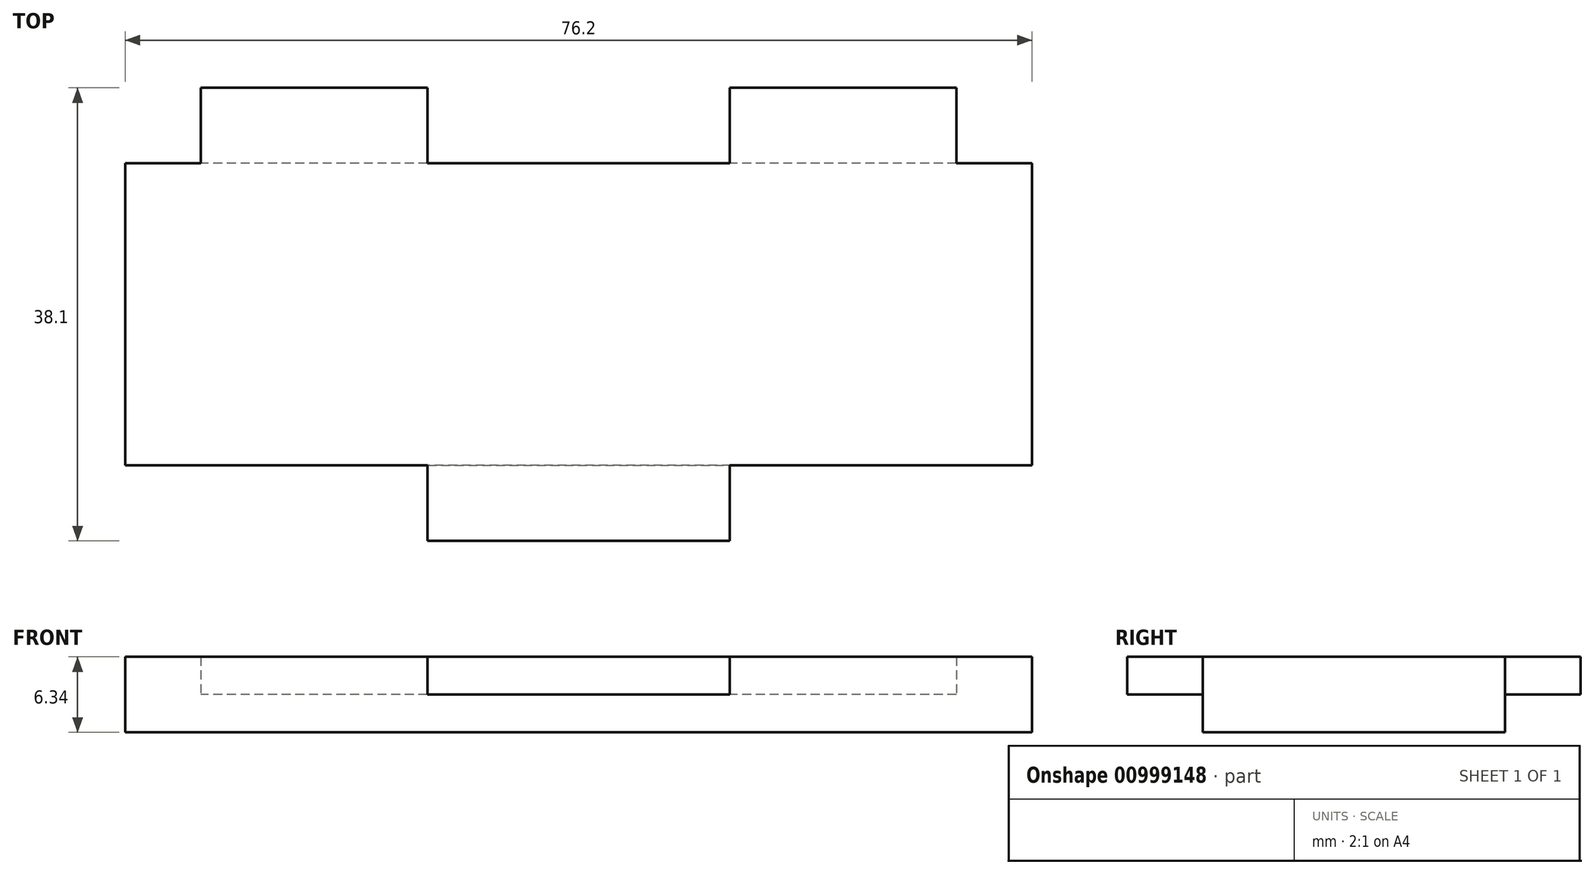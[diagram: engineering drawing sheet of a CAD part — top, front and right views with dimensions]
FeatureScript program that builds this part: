
annotation { "Feature Type Name" : "Feature", "Feature Type Description" : "" }
export const myFeature = defineFeature(function(context is Context, id is Id, definition is map)
    precondition{}
    {
        {
            var Q0;
            Q0=qCreatedBy(makeId("Right.planeOp"),FACE);
            var sketch = newSketch(context, id + "F0", { "sketchPlane" : qUnion([Q0])});
            skLineSegment(sketch, "E0.bottom", {"start": v(12.7, -3.17) * mm, "end": v(-12.7, -3.18) * mm});
            skLineSegment(sketch, "E0.top", {"start": v(12.7, 3.18) * mm, "end": v(-12.7, 3.17) * mm});
            skLineSegment(sketch, "E0.left", {"start": v(12.7, -3.17) * mm, "end": v(12.7, 3.18) * mm});
            skLineSegment(sketch, "E0.right", {"start": v(-12.7, -3.18) * mm, "end": v(-12.7, 3.17) * mm});
            skPoint(sketch, "E0.middle", {"position": v(0, 0) * mm});
            skSolve(sketch);
        }
        {
            var Q0;
            Q0 = qSketchRegion(id + "F0", true);
            extrude(context, id + "F1", {"entities" : qUnion([Q0]), "depth" : 76.2 * mm, "offsetDistance" : 25.4 * mm});
        }
        {
            var Q0;
            Q0=makeQuery(id+"F1.opExtrude","SWEPT_FACE",FACE,{"disambiguationData":[OSD([sQuery(id+"F0.wireOp",EDGE,"E0.right")])]});
            var sketch = newSketch(context, id + "F2", { "sketchPlane" : qUnion([Q0])});
            skLineSegment(sketch, "E1", {"start": v(0, 0) * mm, "end": v(25.4, 0) * mm});
            skLineSegment(sketch, "E2", {"start": v(76.2, 0) * mm, "end": v(50.8, 0) * mm});
            skLineSegment(sketch, "E3.bottom", {"start": v(25.4, 0) * mm, "end": v(50.8, 0) * mm});
            skLineSegment(sketch, "E3.top", {"start": v(25.4, 3.17) * mm, "end": v(50.8, 3.17) * mm});
            skLineSegment(sketch, "E3.left", {"start": v(25.4, 0) * mm, "end": v(25.4, 3.17) * mm});
            skLineSegment(sketch, "E3.right", {"start": v(50.8, 0) * mm, "end": v(50.8, 3.17) * mm});
            skLineSegment(sketch, "E4", {"start": v(16, 0) * mm, "end": v(16, 3.17) * mm});
            skSolve(sketch);
        }
        {
            var Q0;
            Q0=makeQuery(id+"F2.imprint","IMPRINT",FACE,{"disambiguationData":[TD([[makeQuery(id+"F2.imprint","IMPRINT",EDGE,{"derivedFrom":sQuery(id+"F2.wireOp",EDGE,"E3.bottom")}),1.0]])]});
            extrude(context, id + "F3", {"entities" : qUnion([Q0]), "operationType" : NewBodyOperationType.ADD, "depth" : 6.35 * mm, "offsetDistance" : 25.4 * mm});
        }
        {
            var Q0;
            Q0=makeQuery(id+"F1.opExtrude","SWEPT_FACE",FACE,{"disambiguationData":[OSD([sQuery(id+"F0.wireOp",EDGE,"E0.left")])]});
            var sketch = newSketch(context, id + "F4", { "sketchPlane" : qUnion([Q0])});
            skLineSegment(sketch, "E5", {"start": v(-76.2, 0) * mm, "end": v(-69.85, 0) * mm});
            skLineSegment(sketch, "E6", {"start": v(-6.35, 0) * mm, "end": v(0, 0) * mm});
            skLineSegment(sketch, "E7", {"start": v(-38.1, 0) * mm, "end": v(-25.4, 0) * mm});
            skPoint(sketch, "E7.startSnap0", {"position": v(-38.1, 0) * mm});
            skLineSegment(sketch, "E8", {"start": v(-38.1, 0) * mm, "end": v(-50.8, 0) * mm});
            skLineSegment(sketch, "E9", {"start": v(-50.8, 3.17) * mm, "end": v(-50.8, -3.17) * mm});
            skLineSegment(sketch, "E10", {"start": v(-69.85, 3.17) * mm, "end": v(-69.85, -3.17) * mm});
            skLineSegment(sketch, "E11", {"start": v(-25.4, 3.17) * mm, "end": v(-25.4, -3.17) * mm});
            skLineSegment(sketch, "E12", {"start": v(-6.35, 3.17) * mm, "end": v(-6.35, -3.17) * mm});
            skLineSegment(sketch, "E13", {"start": v(-69.85, 0) * mm, "end": v(-50.8, 0) * mm});
            skLineSegment(sketch, "E14", {"start": v(-25.4, 0) * mm, "end": v(-6.35, 0) * mm});
            skLineSegment(sketch, "E15", {"start": v(-38.1, 0) * mm, "end": v(-38.1, 3.18) * mm});
            skSolve(sketch);
        }
        {
            var Q0;
            {var subQ7=sQuery(id+"F4.wireOp",EDGE,"E9");var subQ8=makeQuery(id+"F4.imprint","INTERSECT",VERTEX,{"derivedFrom":[sQuery(id+"F4.wireOp",EDGE,"E8"),subQ7]});Q0=makeQuery(id+"F4.imprint","IMPRINT",FACE,{"disambiguationData":[TD([[makeQuery(id+"F4.imprint","IMPRINT",EDGE,{"disambiguationData":[TD([[subQ8,1.0]])],"derivedFrom":subQ7}),-1.0]])]});}
            var Q1;
            {var subQ7=sQuery(id+"F4.wireOp",EDGE,"E11");var subQ8=makeQuery(id+"F4.imprint","INTERSECT",VERTEX,{"derivedFrom":[sQuery(id+"F4.wireOp",EDGE,"E7"),subQ7]});Q1=makeQuery(id+"F4.imprint","IMPRINT",FACE,{"disambiguationData":[TD([[makeQuery(id+"F4.imprint","IMPRINT",EDGE,{"disambiguationData":[TD([[subQ8,1.0]])],"derivedFrom":subQ7}),1.0]])]});}
            extrude(context, id + "F5", {"entities" : qUnion([Q0, Q1]), "operationType" : NewBodyOperationType.ADD, "depth" : 6.35 * mm, "offsetDistance" : 25.4 * mm});
        }
    });
